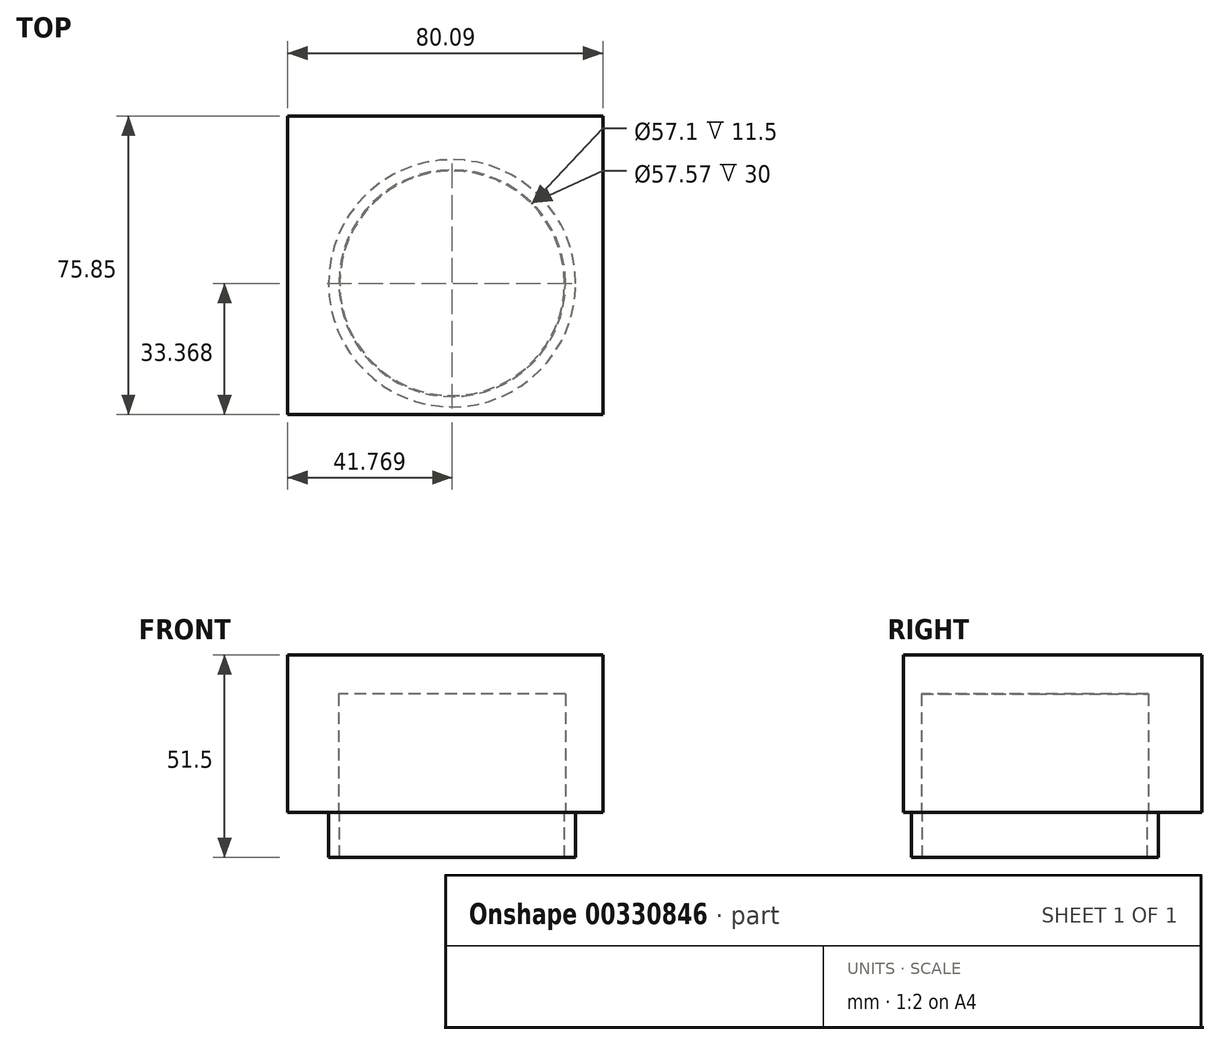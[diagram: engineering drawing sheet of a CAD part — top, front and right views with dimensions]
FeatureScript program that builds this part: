
annotation { "Feature Type Name" : "Feature", "Feature Type Description" : "" }
export const myFeature = defineFeature(function(context is Context, id is Id, definition is map)
    precondition{}
    {
        {
            var Q0;
            Q0=qCreatedBy(makeId("Top.planeOp"),FACE);
            var sketch = newSketch(context, id + "F0", { "sketchPlane" : qUnion([Q0])});
            skLineSegment(sketch, "E0.bottom", {"start": v(-49.45, 21.36) * mm, "end": v(30.64, 21.36) * mm});
            skLineSegment(sketch, "E0.top", {"start": v(-49.45, -54.5) * mm, "end": v(30.64, -54.5) * mm});
            skLineSegment(sketch, "E0.left", {"start": v(-49.45, 21.36) * mm, "end": v(-49.45, -54.5) * mm});
            skLineSegment(sketch, "E0.right", {"start": v(30.64, 21.36) * mm, "end": v(30.64, -54.5) * mm});
            skSolve(sketch);
        }
        {
            var Q0;
            Q0=makeQuery(id+"F0.imprint","IMPRINT",FACE,{"disambiguationData":[TD([[makeQuery(id+"F0.imprint","IMPRINT",EDGE,{"derivedFrom":sQuery(id+"F0.wireOp",EDGE,"E0.bottom")}),-1.0]])]});
            extrude(context, id + "F1", {"entities" : qUnion([Q0]), "depth" : 40 * mm});
        }
        {
            var Q0;
            Q0=qCreatedBy(makeId("Top.planeOp"),FACE);
            var sketch = newSketch(context, id + "F2", { "sketchPlane" : qUnion([Q0])});
            skCircle(sketch, "E1", {"center": v(-7.68, -21.12) * mm, "radius": 28.78 * mm});
            skSolve(sketch);
        }
        {
            var Q0;
            Q0 = qSketchRegion(id + "F2", true);
            extrude(context, id + "F3", {"entities" : qUnion([Q0]), "operationType" : NewBodyOperationType.REMOVE, "depth" : 30 * mm});
        }
        {
            var Q0;
            Q0=makeQuery(id+"F1.opExtrude","CAP_FACE",FACE,{"disambiguationData":[OSD([sQuery(id+"F0.wireOp",EDGE,"E0.bottom"),sQuery(id+"F0.wireOp",EDGE,"E0.top"),sQuery(id+"F0.wireOp",EDGE,"E0.left"),sQuery(id+"F0.wireOp",EDGE,"E0.right")])],"isStart":true});
            var sketch = newSketch(context, id + "F4", { "sketchPlane" : qUnion([Q0])});
            skCircle(sketch, "E2", {"center": v(-5.93, 24.98) * mm, "radius": 2.8 * mm});
            skCircle(sketch, "E3", {"center": v(-7.68, 21.12) * mm, "radius": 28.55 * mm});
            skCircle(sketch, "E4", {"center": v(-7.68, 21.12) * mm, "radius": 31.4 * mm});
            skSolve(sketch);
        }
        {
            var Q0;
            Q0 = qSketchRegion(id + "F4", true);
            extrude(context, id + "F5", {"entities" : qUnion([Q0]), "operationType" : NewBodyOperationType.ADD, "depth" : 11.5 * mm});
        }
    });
